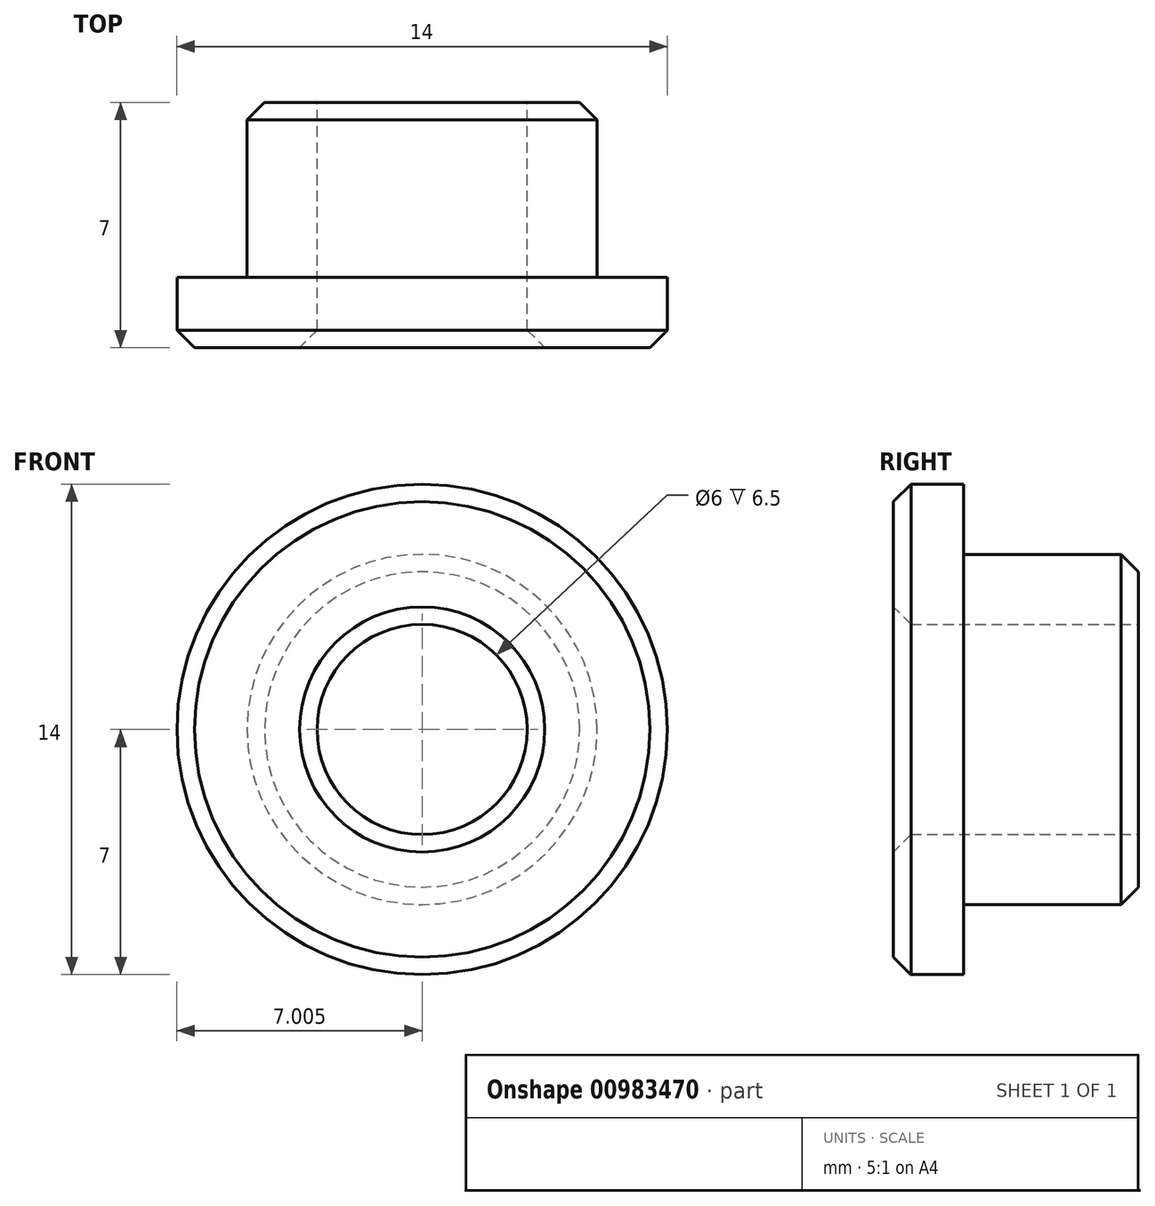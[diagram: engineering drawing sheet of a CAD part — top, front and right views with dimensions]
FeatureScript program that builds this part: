
annotation { "Feature Type Name" : "Feature", "Feature Type Description" : "" }
export const myFeature = defineFeature(function(context is Context, id is Id, definition is map)
    precondition{}
    {
        {
            var Q0;
            Q0=qCreatedBy(makeId("Front.planeOp"),FACE);
            var sketch = newSketch(context, id + "F0", { "sketchPlane" : qUnion([Q0])});
            skCircle(sketch, "E0", {"center": v(1.21, 0) * mm, "radius": 5 * mm});
            skCircle(sketch, "E1", {"center": v(1.21, 0) * mm, "radius": 3 * mm});
            skSolve(sketch);
        }
        {
            var Q0;
            Q0=qSketchRegion(id+"F0",true);
            extrude(context, id + "F1", {"entities" : qUnion([Q0]), "depth" : 5 * mm});
        }
        {
            var Q0;
            Q0=makeQuery(id+"F1.opExtrude","CAP_FACE",FACE,{"disambiguationData":[OSD([sQuery(id+"F0.wireOp",EDGE,"E0"),sQuery(id+"F0.wireOp",EDGE,"E1")])],"isStart":false});
            var sketch = newSketch(context, id + "F2", { "sketchPlane" : qUnion([Q0])});
            skCircle(sketch, "E2.0", {"center": v(1.21, 0) * mm, "radius": 7 * mm});
            skSolve(sketch);
        }
        {
            var Q0;
            Q0=makeQuery(id+"F2.imprint","IMPRINT",FACE,{"disambiguationData":[TD([[makeQuery(id+"F2.imprint","IMPRINT",EDGE,{"derivedFrom":sQuery(id+"F2.wireOp",EDGE,"E2.0")}),1.0]])]});
            var Q1;
            Q1=makeQuery(id+"F2.imprint","IMPRINT",FACE,{"disambiguationData":[TD([[makeQuery(id+"F2.imprint","IMPRINT",EDGE,{"derivedFrom":makeQuery(id+"F1.opExtrude","CAP_EDGE",EDGE,{"disambiguationData":[OSD([sQuery(id+"F0.wireOp",EDGE,"E0")])],"isStart":false})}),1.0]])]});
            extrude(context, id + "F3", {"entities" : qUnion([Q0, Q1]), "operationType" : NewBodyOperationType.ADD, "depth" : 2 * mm});
        }
        {
            var Q0;
            Q0=makeQuery(id+"F3.opExtrude","CAP_EDGE",EDGE,{"disambiguationData":[OSD([sQuery(id+"F0.wireOp",EDGE,"E1")])],"isStart":false});
            chamfer(context, id + "F4", {"entities" : qUnion([Q0]), "width" : 0.5 * mm, "tangentPropagation" : true});
        }
        {
            var Q0;
            Q0=makeQuery(id+"F3.opExtrude","CAP_EDGE",EDGE,{"disambiguationData":[OSD([sQuery(id+"F2.wireOp",EDGE,"E2.0")])],"isStart":false});
            chamfer(context, id + "F5", {"entities" : qUnion([Q0]), "width" : 0.5 * mm, "tangentPropagation" : true});
        }
        {
            var Q0;
            Q0=makeQuery(id+"F1.opExtrude","CAP_EDGE",EDGE,{"disambiguationData":[OSD([sQuery(id+"F0.wireOp",EDGE,"E0")])],"isStart":true});
            chamfer(context, id + "F6", {"entities" : qUnion([Q0]), "width" : 0.5 * mm, "tangentPropagation" : true});
        }
    });
